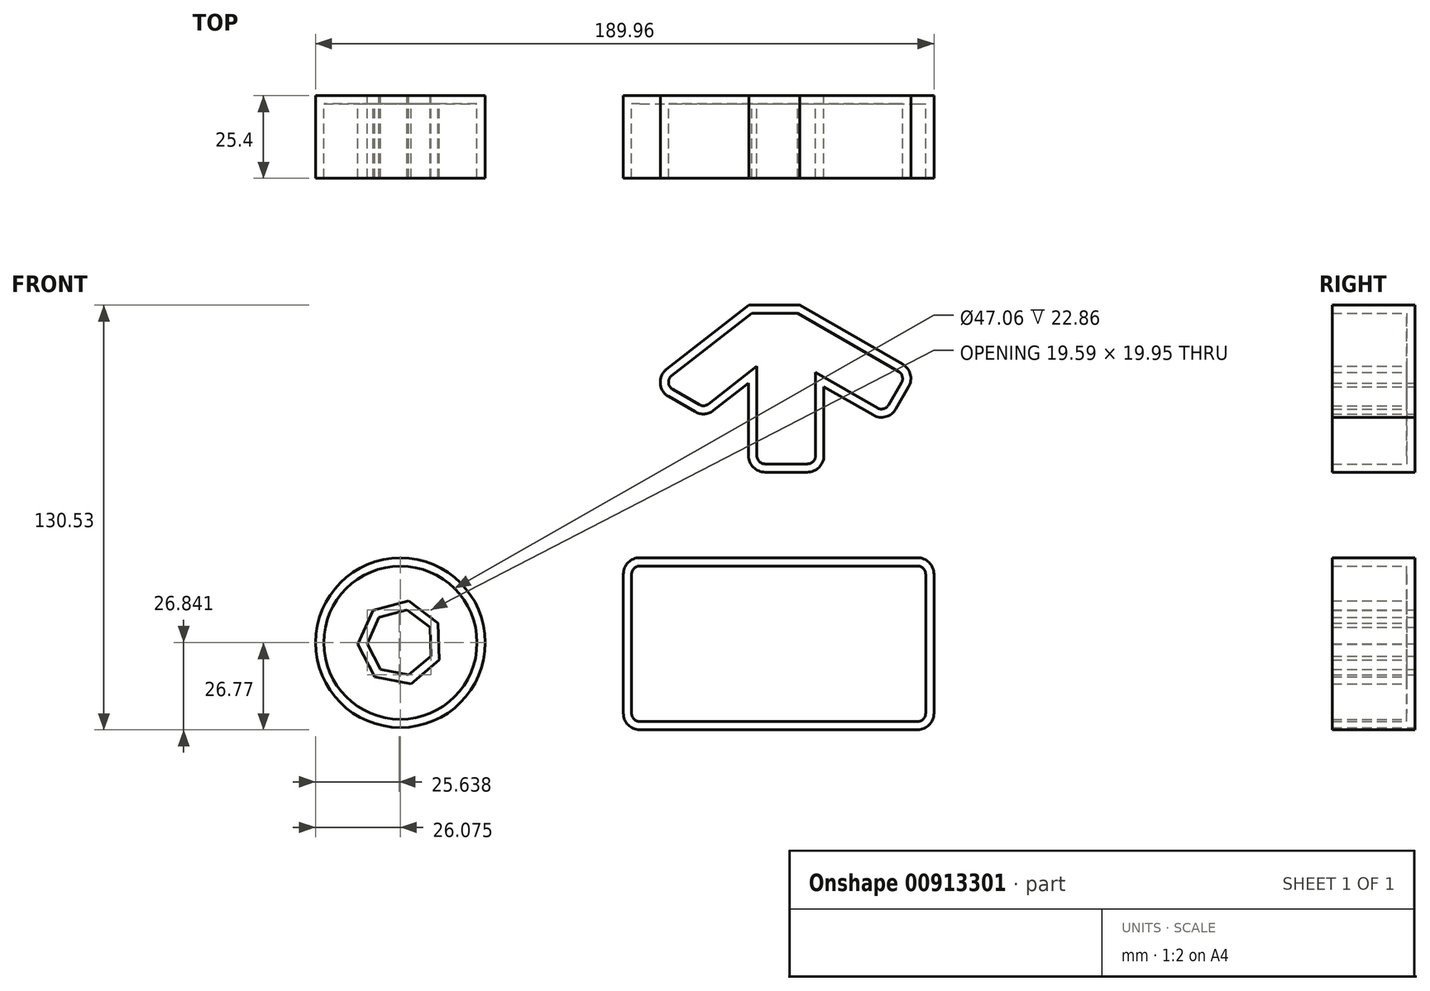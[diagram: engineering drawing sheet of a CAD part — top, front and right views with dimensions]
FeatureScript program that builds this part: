
annotation { "Feature Type Name" : "Feature", "Feature Type Description" : "" }
export const myFeature = defineFeature(function(context is Context, id is Id, definition is map)
    precondition{}
    {
        {
            var Q0;
            Q0=qCreatedBy(makeId("Front.planeOp"),FACE);
            var sketch = newSketch(context, id + "F0", { "sketchPlane" : qUnion([Q0])});
            skLineSegment(sketch, "E0.bottom", {"start": v(-54.2, 17.5) * mm, "end": v(41.19, 17.5) * mm});
            skLineSegment(sketch, "E0.top", {"start": v(-54.2, -35.4) * mm, "end": v(41.19, -35.4) * mm});
            skLineSegment(sketch, "E0.left", {"start": v(-54.2, 17.5) * mm, "end": v(-54.2, -35.4) * mm});
            skLineSegment(sketch, "E0.right", {"start": v(41.19, 17.5) * mm, "end": v(41.19, -35.4) * mm});
            skLineSegment(sketch, "E1", {"start": v(-15.75, 43.8) * mm, "end": v(7.38, 43.8) * mm});
            skLineSegment(sketch, "E2", {"start": v(7.38, 43.8) * mm, "end": v(7.38, 70.05) * mm});
            skLineSegment(sketch, "E3", {"start": v(7.38, 70.05) * mm, "end": v(26.95, 58.8) * mm});
            skLineSegment(sketch, "E4", {"start": v(26.95, 58.8) * mm, "end": v(35.95, 74.45) * mm});
            skLineSegment(sketch, "E5", {"start": v(35.95, 74.45) * mm, "end": v(0, 95.13) * mm});
            skLineSegment(sketch, "E6", {"start": v(0, 95.13) * mm, "end": v(-15.64, 95.13) * mm});
            skLineSegment(sketch, "E7", {"start": v(-15.64, 95.13) * mm, "end": v(-46.9, 70.82) * mm});
            skLineSegment(sketch, "E8", {"start": v(-46.9, 70.82) * mm, "end": v(-29.21, 60.65) * mm});
            skLineSegment(sketch, "E9", {"start": v(-29.21, 60.65) * mm, "end": v(-15.75, 71.13) * mm});
            skLineSegment(sketch, "E10", {"start": v(-15.75, 71.13) * mm, "end": v(-15.75, 43.8) * mm});
            skFitSpline(sketch, "E11", {"points": [v(-97.26, 53.51) * mm, v(-103.91, 37.14) * mm, v(-97.2, 31) * mm, v(-97.99, 16.7) * mm, v(-109.3, 17.8) * mm], "startDerivative": vector(-41.21, -67.19) * mm, "endDerivative": vector(-56.3, 22.05) * mm});
            skLineSegment(sketch, "E12", {"start": v(-90.36, 54.53) * mm, "end": v(-88.56, 14.56) * mm, "construction": true});
            skFitSpline(sketch, "E13.MirrorCS", {"points": [v(-83.39, 54.13) * mm, v(-75.3, 38.42) * mm, v(-81.44, 31.71) * mm, v(-79.36, 17.54) * mm, v(-68.2, 19.65) * mm], "startDerivative": vector(47.07, -63.22) * mm, "endDerivative": vector(54.1, 27.01) * mm});
            skCircle(sketch, "E14.cCircle", {"center": v(-122.7, -8.63) * mm, "radius": 9.22 * mm, "construction": true});
            skLineSegment(sketch, "E14.0", {"start": v(-113.34, -12.78) * mm, "end": v(-120.1, -18.53) * mm});
            skLineSegment(sketch, "E14.1", {"start": v(-120.1, -18.53) * mm, "end": v(-128.82, -16.83) * mm});
            skLineSegment(sketch, "E14.2", {"start": v(-128.82, -16.83) * mm, "end": v(-132.93, -8.95) * mm});
            skLineSegment(sketch, "E14.3", {"start": v(-132.93, -8.95) * mm, "end": v(-129.32, -0.83) * mm});
            skLineSegment(sketch, "E14.4", {"start": v(-129.32, -0.83) * mm, "end": v(-120.73, 1.42) * mm});
            skLineSegment(sketch, "E14.5", {"start": v(-120.73, 1.42) * mm, "end": v(-113.62, -3.9) * mm});
            skLineSegment(sketch, "E14.6", {"start": v(-113.62, -3.9) * mm, "end": v(-113.34, -12.78) * mm});
            skPoint(sketch, "E14.0.midPoint", {"position": v(-116.72, -15.66) * mm});
            skCircle(sketch, "E15", {"center": v(-122.7, -8.63) * mm, "radius": 26.07 * mm});
            skSolve(sketch);
        }
        {
            var Q0;
            Q0=makeQuery(id+"F0.imprint","IMPRINT",FACE,{"disambiguationData":[TD([[makeQuery(id+"F0.imprint","IMPRINT",EDGE,{"derivedFrom":sQuery(id+"F0.wireOp",EDGE,"E0.bottom")}),-1.0]])]});
            var Q1;
            Q1=makeQuery(id+"F0.imprint","IMPRINT",FACE,{"disambiguationData":[TD([[makeQuery(id+"F0.imprint","IMPRINT",EDGE,{"derivedFrom":sQuery(id+"F0.wireOp",EDGE,"E1")}),1.0]])]});
            var Q2;
            Q2=makeQuery(id+"F0.imprint","IMPRINT",FACE,{"disambiguationData":[TD([[makeQuery(id+"F0.imprint","IMPRINT",EDGE,{"derivedFrom":sQuery(id+"F0.wireOp",EDGE,"E14.0")}),1.0]])]});
            extrude(context, id + "F1", {"entities" : qUnion([Q0, Q1, Q2]), "depth" : 25.4 * mm, "offsetDistance" : 25.4 * mm});
        }
        {
            var Q0;
            Q0=makeQuery(id+"F1.opExtrude","SWEPT_EDGE",EDGE,{"disambiguationData":[OSD([sQuery(id+"F0.wireOp",EDGE,"E0.bottom"),sQuery(id+"F0.wireOp",EDGE,"E0.right")])]});
            var Q1;
            Q1=makeQuery(id+"F1.opExtrude","SWEPT_EDGE",EDGE,{"disambiguationData":[OSD([sQuery(id+"F0.wireOp",EDGE,"E0.bottom"),sQuery(id+"F0.wireOp",EDGE,"E0.left")])]});
            var Q2;
            Q2=makeQuery(id+"F1.opExtrude","SWEPT_EDGE",EDGE,{"disambiguationData":[OSD([sQuery(id+"F0.wireOp",EDGE,"E0.top"),sQuery(id+"F0.wireOp",EDGE,"E0.right")])]});
            var Q3;
            Q3=makeQuery(id+"F1.opExtrude","SWEPT_EDGE",EDGE,{"disambiguationData":[OSD([sQuery(id+"F0.wireOp",EDGE,"E0.top"),sQuery(id+"F0.wireOp",EDGE,"E0.left")])]});
            var Q4;
            Q4=makeQuery(id+"F1.opExtrude","SWEPT_EDGE",EDGE,{"disambiguationData":[OSD([sQuery(id+"F0.wireOp",EDGE,"E1"),sQuery(id+"F0.wireOp",EDGE,"E10")])]});
            var Q5;
            Q5=makeQuery(id+"F1.opExtrude","SWEPT_EDGE",EDGE,{"disambiguationData":[OSD([sQuery(id+"F0.wireOp",EDGE,"E1"),sQuery(id+"F0.wireOp",EDGE,"E2")])]});
            var Q6;
            Q6=makeQuery(id+"F1.opExtrude","SWEPT_EDGE",EDGE,{"disambiguationData":[OSD([sQuery(id+"F0.wireOp",EDGE,"E8"),sQuery(id+"F0.wireOp",EDGE,"E9")])]});
            var Q7;
            Q7=makeQuery(id+"F1.opExtrude","SWEPT_EDGE",EDGE,{"disambiguationData":[OSD([sQuery(id+"F0.wireOp",EDGE,"E7"),sQuery(id+"F0.wireOp",EDGE,"E8")])]});
            var Q8;
            Q8=makeQuery(id+"F1.opExtrude","SWEPT_EDGE",EDGE,{"disambiguationData":[OSD([sQuery(id+"F0.wireOp",EDGE,"E3"),sQuery(id+"F0.wireOp",EDGE,"E4")])]});
            var Q9;
            Q9=makeQuery(id+"F1.opExtrude","SWEPT_EDGE",EDGE,{"disambiguationData":[OSD([sQuery(id+"F0.wireOp",EDGE,"E4"),sQuery(id+"F0.wireOp",EDGE,"E5")])]});
            fillet(context, id + "F2", {"entities" : qUnion([Q0, Q1, Q2, Q3, Q4, Q5, Q6, Q7, Q8, Q9]), "radius" : 5.08 * mm, "tangentPropagation" : true, "allowEdgeOverflow" : false});
        }
        {
            var Q0;
            Q0=makeQuery(id+"F1.opExtrude","CAP_FACE",FACE,{"disambiguationData":[OSD([sQuery(id+"F0.wireOp",EDGE,"E0.bottom"),sQuery(id+"F0.wireOp",EDGE,"E0.top"),sQuery(id+"F0.wireOp",EDGE,"E0.left"),sQuery(id+"F0.wireOp",EDGE,"E0.right")])],"isStart":false});
            var Q1;
            Q1=makeQuery(id+"F1.opExtrude","CAP_FACE",FACE,{"disambiguationData":[OSD([sQuery(id+"F0.wireOp",EDGE,"E1"),sQuery(id+"F0.wireOp",EDGE,"E2"),sQuery(id+"F0.wireOp",EDGE,"E3"),sQuery(id+"F0.wireOp",EDGE,"E4"),sQuery(id+"F0.wireOp",EDGE,"E5"),sQuery(id+"F0.wireOp",EDGE,"E6"),sQuery(id+"F0.wireOp",EDGE,"E7"),sQuery(id+"F0.wireOp",EDGE,"E8"),sQuery(id+"F0.wireOp",EDGE,"E9"),sQuery(id+"F0.wireOp",EDGE,"E10")])],"isStart":false});
            var Q2;
            Q2=makeQuery(id+"F1.opExtrude","CAP_FACE",FACE,{"disambiguationData":[OSD([sQuery(id+"F0.wireOp",EDGE,"E14.0"),sQuery(id+"F0.wireOp",EDGE,"E14.1"),sQuery(id+"F0.wireOp",EDGE,"E14.2"),sQuery(id+"F0.wireOp",EDGE,"E14.3"),sQuery(id+"F0.wireOp",EDGE,"E14.4"),sQuery(id+"F0.wireOp",EDGE,"E14.5"),sQuery(id+"F0.wireOp",EDGE,"E14.6"),sQuery(id+"F0.wireOp",EDGE,"E15")])],"isStart":false});
            shell(context, id + "F3", {"entities" : qUnion([Q0, Q1, Q2]), "thickness" : 2.54 * mm});
        }
    });
